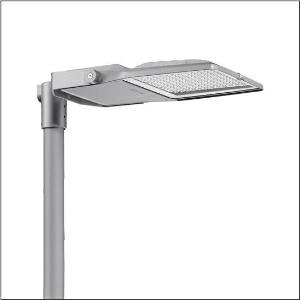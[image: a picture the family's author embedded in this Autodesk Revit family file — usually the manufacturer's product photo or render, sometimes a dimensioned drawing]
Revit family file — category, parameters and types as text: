
# Revit family: floodlight_fl_21_iq_midi___pl33t_5xa7782e4f3a_344b
name_source: partatom
category: Lighting Fixtures
units: mm (PartAtom-declared; Revit-internal decimal feet)

## family parameters
Cut with Voids When Loaded = No
Host = Face
Light Source = No
Part Type = Normal
Room Calculation Point = No
Round Connector Dimension = Use Diameter
Shared = No

## types (1)
- --- (1 x LED, 27690 lm, 208.1 W, 4000K)
    Apparent Load = 208 VA
    CIE Flux Codes = 26 75 99 100 100
    Color Rendering = 70
    Color Temperature = 4000K
    Default Elevation = 1800 mm
    Description = Floodlight FL 21 iQ midi, floodlight, primary light control with lens, of PMMA, primary optical cover: protective disc, of toughened safety glass, transparent, light distribution: PL33T, light emission: direct distribution, installation type: surface-mounted, LED, High Power LED, rated luminous flux: 27.690lm, luminous efficacy: 133lm/W, light colour: 740, colour temperature: 4000K, control gear: ECG iQ, control: optimised constant luminous flux control (CLO 2.0), Desk-Remote (wireless, voltage-free reading and setting of iQ features in the workshop via application-optimized NFC function/RFID function), Smart-Wire, Night-Set, Temp-Guard, Auto-Match, Street-Remote, with terminal, 6-pole, mains connection: 220..240V, AC, 50/60Hz, start of lifetime: 208W, end of service life: 227W, reduction: 90W, luminaire housing, of diecast aluminium, powder-coated, Siteco® metallic grey (DB 702S), corrosivity category C5 mid according to DIN EN ISO 12944, sealing non-destructively replaceable, please order mast flange separately, mast bracket, of steel, galvanised, powder-coated, Siteco® metallic grey (DB 702S), protection rating (complete): IP66, insulation class (complete): insulation class II (safety insulation), certification: CE, ENEC, VDE, protection symbol: D, impact resistance: IK08, permissible operating ambient temperature: -40..+40°C, permissible operating ambient temperature for outdoor applications: -40..+50°C, standard: DIN EN 12944, LABS conformity tested according to VDMA 24364:2018-05, packaging unit: 1 piece

Light Distribution: PL33T
    Height = 76 mm
    Lamp = 1 x LED
    Lamp Light Flux = 27690 lm
    Lamp Power = 208.1 W
    Lamp count = 1
    Length = 657 mm
    Luminous efficacy = 133 lm/W
    Manufacturer = Siteco
    ModVariant = No
    Model = 5XA7782E4F3A
    Number of Poles = 1
    OnlyDefault = Yes
    Power Factor = 1
    Product Name = Floodlight FL 21 iQ midi | PL33T
    Product group = floodlight | pylon annexe
    ProductGroupID = 6200
    Protection Class = Protection class II
    Protection Degree = IP 66
    RLX_Detail_Level = 1
    RLX_Emergency_Light_Flux = 0 lm
    RLX_Emergency_Type = 0
    RLX_Emergency_Type_DB = No
    RlxData = <blob elided: 153677 chars, md5=d895bb24>
    Socket = socket
    Standby Power = 0 W
    System Light Flux = 27690 lm
    System Power = 208 W
    Type Comments = factory setting: luminous flux: 100 % | dim-lin: 254 | 710 mA
    Type Image = l_1007123.jpg
    URL = http://relux.com
    VarID = @adj_072563
    Voltage = 0 V
    Weight = 0.00 kg
    Width = 442 mm

## geometry (parser evidence)
native form markers: Blend x4, Sweep x13
no freeform markers — native parametric forms only
